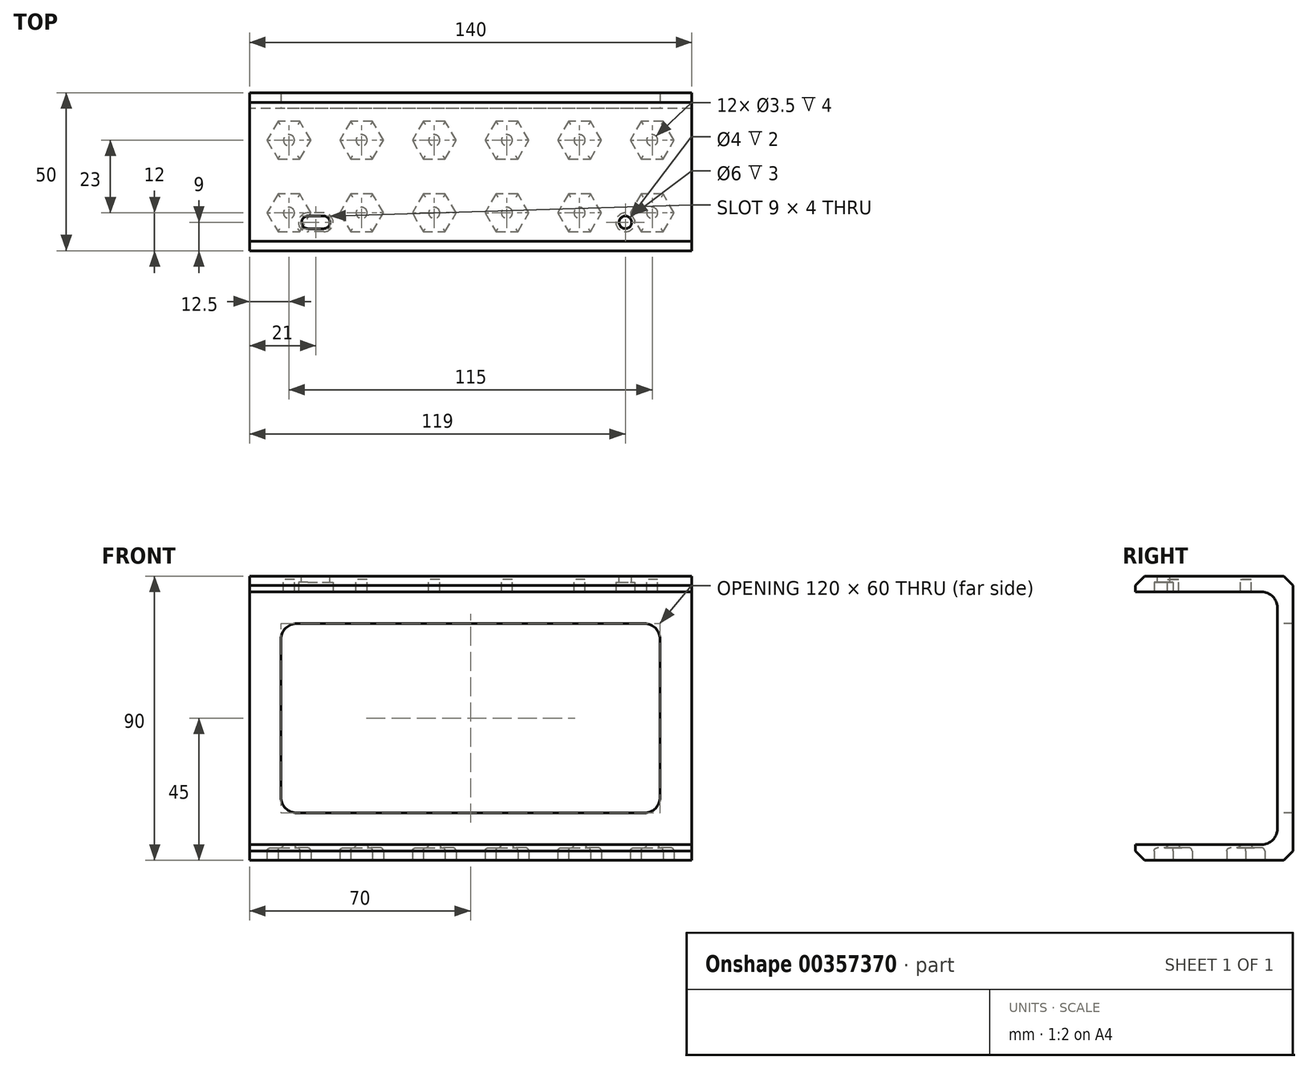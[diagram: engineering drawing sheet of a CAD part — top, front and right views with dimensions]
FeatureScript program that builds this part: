
annotation { "Feature Type Name" : "Feature", "Feature Type Description" : "" }
export const myFeature = defineFeature(function(context is Context, id is Id, definition is map)
    precondition{}
    {
        {
            var Q0;
            Q0=qCreatedBy(makeId("Right.planeOp"),FACE);
            var sketch = newSketch(context, id + "F0", { "sketchPlane" : qUnion([Q0])});
            skLineSegment(sketch, "E0", {"start": v(-50, 0) * mm, "end": v(0, 0) * mm});
            skLineSegment(sketch, "E1", {"start": v(0, 0) * mm, "end": v(0, 90) * mm});
            skLineSegment(sketch, "E2", {"start": v(0, 90) * mm, "end": v(-50, 90) * mm});
            skLineSegment(sketch, "E3", {"start": v(-50, 90) * mm, "end": v(-50, 85) * mm});
            skLineSegment(sketch, "E4", {"start": v(-50, 85) * mm, "end": v(-5, 85) * mm});
            skLineSegment(sketch, "E5", {"start": v(-5, 85) * mm, "end": v(-5, 5) * mm});
            skLineSegment(sketch, "E6", {"start": v(-5, 5) * mm, "end": v(-50, 5) * mm});
            skLineSegment(sketch, "E7", {"start": v(-50, 5) * mm, "end": v(-50, 0) * mm});
            skSolve(sketch);
        }
        {
            var Q0;
            Q0 = qSketchRegion(id + "F0", true);
            extrude(context, id + "F1", {"entities" : qUnion([Q0]), "depth" : 140 * mm});
        }
        {
            var Q0;
            Q0=makeQuery(id+"F1.opExtrude","SWEPT_FACE",FACE,{"disambiguationData":[OSD([sQuery(id+"F0.wireOp",EDGE,"E2")])]});
            cPlane(context, id + "F2", {"entities" : qUnion([Q0]), "cplaneType" : CPlaneType.OFFSET, "offset" : 1 * mm, "oppositeDirection" : true, "width" : 150 * mm, "height" : 150 * mm});
        }
        {
            var Q0;
            Q0=qCreatedBy(id+"F2.planeOp",FACE);
            var sketch = newSketch(context, id + "F3", { "sketchPlane" : qUnion([Q0])});
            skCircle(sketch, "E8", {"center": v(12.5, -38) * mm, "radius": 1.75 * mm});
            skCircle(sketch, "E9", {"center": v(12.5, -38) * mm, "radius": 10 * mm, "construction": true});
            skCircle(sketch, "E10.0.1.0", {"center": v(12.5, -15) * mm, "radius": 10 * mm, "construction": true});
            skCircle(sketch, "E10.0.1.1", {"center": v(12.5, -15) * mm, "radius": 1.75 * mm});
            skCircle(sketch, "E10.1.0.0", {"center": v(35.5, -38) * mm, "radius": 10 * mm, "construction": true});
            skCircle(sketch, "E10.1.0.1", {"center": v(35.5, -38) * mm, "radius": 1.75 * mm});
            skCircle(sketch, "E10.1.1.0", {"center": v(35.5, -15) * mm, "radius": 10 * mm, "construction": true});
            skCircle(sketch, "E10.1.1.1", {"center": v(35.5, -15) * mm, "radius": 1.75 * mm});
            skCircle(sketch, "E10.2.0.0", {"center": v(58.5, -38) * mm, "radius": 10 * mm, "construction": true});
            skCircle(sketch, "E10.2.0.1", {"center": v(58.5, -38) * mm, "radius": 1.75 * mm});
            skCircle(sketch, "E10.2.1.0", {"center": v(58.5, -15) * mm, "radius": 10 * mm, "construction": true});
            skCircle(sketch, "E10.2.1.1", {"center": v(58.5, -15) * mm, "radius": 1.75 * mm});
            skCircle(sketch, "E10.3.0.0", {"center": v(81.5, -38) * mm, "radius": 10 * mm, "construction": true});
            skCircle(sketch, "E10.3.0.1", {"center": v(81.5, -38) * mm, "radius": 1.75 * mm});
            skCircle(sketch, "E10.3.1.0", {"center": v(81.5, -15) * mm, "radius": 10 * mm, "construction": true});
            skCircle(sketch, "E10.3.1.1", {"center": v(81.5, -15) * mm, "radius": 1.75 * mm});
            skCircle(sketch, "E10.4.0.0", {"center": v(104.5, -38) * mm, "radius": 10 * mm, "construction": true});
            skCircle(sketch, "E10.4.0.1", {"center": v(104.5, -38) * mm, "radius": 1.75 * mm});
            skCircle(sketch, "E10.4.1.0", {"center": v(104.5, -15) * mm, "radius": 10 * mm, "construction": true});
            skCircle(sketch, "E10.4.1.1", {"center": v(104.5, -15) * mm, "radius": 1.75 * mm});
            skCircle(sketch, "E10.5.0.0", {"center": v(127.5, -38) * mm, "radius": 10 * mm, "construction": true});
            skCircle(sketch, "E10.5.0.1", {"center": v(127.5, -38) * mm, "radius": 1.75 * mm});
            skCircle(sketch, "E10.5.1.0", {"center": v(127.5, -15) * mm, "radius": 10 * mm, "construction": true});
            skCircle(sketch, "E10.5.1.1", {"center": v(127.5, -15) * mm, "radius": 1.75 * mm});
            skLineSegment(sketch, "E10.direction1", {"start": v(12.5, -38) * mm, "end": v(35.5, -38) * mm, "construction": true});
            skLineSegment(sketch, "E10.direction2", {"start": v(12.5, -38) * mm, "end": v(12.5, -15) * mm, "construction": true});
            skLineSegment(sketch, "E11", {"start": v(70, 0) * mm, "end": v(70, -80.44) * mm, "construction": true});
            skSolve(sketch);
        }
        {
            var Q0;
            Q0 = qSketchRegion(id + "F3", true);
            extrude(context, id + "F4", {"entities" : qUnion([Q0]), "operationType" : NewBodyOperationType.REMOVE, "endBound" : BoundingType.THROUGH_ALL, "oppositeDirection" : true, "depth" : 25 * mm});
        }
        {
            var Q0;
            Q0=makeQuery(id+"F1.opExtrude","SWEPT_FACE",FACE,{"disambiguationData":[OSD([sQuery(id+"F0.wireOp",EDGE,"E0")])]});
            var sketch = newSketch(context, id + "F5", { "sketchPlane" : qUnion([Q0])});
            skCircle(sketch, "E12.cCircle", {"center": v(12.5, 15) * mm, "radius": 6 * mm, "construction": true});
            skLineSegment(sketch, "E12.0", {"start": v(19.43, 15) * mm, "end": v(15.96, 9) * mm});
            skLineSegment(sketch, "E12.1", {"start": v(15.96, 9) * mm, "end": v(9.04, 9) * mm});
            skLineSegment(sketch, "E12.2", {"start": v(9.04, 9) * mm, "end": v(5.57, 15) * mm});
            skLineSegment(sketch, "E12.3", {"start": v(5.57, 15) * mm, "end": v(9.04, 21) * mm});
            skLineSegment(sketch, "E12.4", {"start": v(9.04, 21) * mm, "end": v(15.96, 21) * mm});
            skLineSegment(sketch, "E12.5", {"start": v(15.96, 21) * mm, "end": v(19.43, 15) * mm});
            skPoint(sketch, "E12.0.midPoint", {"position": v(17.7, 12) * mm});
            skLineSegment(sketch, "E13.0.1.0", {"start": v(9.04, 32) * mm, "end": v(5.57, 38) * mm});
            skLineSegment(sketch, "E13.0.1.1", {"start": v(15.96, 32) * mm, "end": v(9.04, 32) * mm});
            skCircle(sketch, "E13.0.1.2", {"center": v(12.5, 38) * mm, "radius": 6 * mm, "construction": true});
            skLineSegment(sketch, "E13.0.1.3", {"start": v(19.43, 38) * mm, "end": v(15.96, 32) * mm});
            skLineSegment(sketch, "E13.0.1.4", {"start": v(15.96, 44) * mm, "end": v(19.43, 38) * mm});
            skLineSegment(sketch, "E13.0.1.5", {"start": v(9.04, 44) * mm, "end": v(15.96, 44) * mm});
            skLineSegment(sketch, "E13.0.1.6", {"start": v(5.57, 38) * mm, "end": v(9.04, 44) * mm});
            skLineSegment(sketch, "E13.1.0.0", {"start": v(32.04, 9) * mm, "end": v(28.57, 15) * mm});
            skLineSegment(sketch, "E13.1.0.1", {"start": v(38.96, 9) * mm, "end": v(32.04, 9) * mm});
            skCircle(sketch, "E13.1.0.2", {"center": v(35.5, 15) * mm, "radius": 6 * mm, "construction": true});
            skLineSegment(sketch, "E13.1.0.3", {"start": v(42.43, 15) * mm, "end": v(38.96, 9) * mm});
            skLineSegment(sketch, "E13.1.0.4", {"start": v(38.96, 21) * mm, "end": v(42.43, 15) * mm});
            skLineSegment(sketch, "E13.1.0.5", {"start": v(32.04, 21) * mm, "end": v(38.96, 21) * mm});
            skLineSegment(sketch, "E13.1.0.6", {"start": v(28.57, 15) * mm, "end": v(32.04, 21) * mm});
            skLineSegment(sketch, "E13.1.1.0", {"start": v(32.04, 32) * mm, "end": v(28.57, 38) * mm});
            skLineSegment(sketch, "E13.1.1.1", {"start": v(38.96, 32) * mm, "end": v(32.04, 32) * mm});
            skCircle(sketch, "E13.1.1.2", {"center": v(35.5, 38) * mm, "radius": 6 * mm, "construction": true});
            skLineSegment(sketch, "E13.1.1.3", {"start": v(42.43, 38) * mm, "end": v(38.96, 32) * mm});
            skLineSegment(sketch, "E13.1.1.4", {"start": v(38.96, 44) * mm, "end": v(42.43, 38) * mm});
            skLineSegment(sketch, "E13.1.1.5", {"start": v(32.04, 44) * mm, "end": v(38.96, 44) * mm});
            skLineSegment(sketch, "E13.1.1.6", {"start": v(28.57, 38) * mm, "end": v(32.04, 44) * mm});
            skLineSegment(sketch, "E13.2.0.0", {"start": v(55.04, 9) * mm, "end": v(51.57, 15) * mm});
            skLineSegment(sketch, "E13.2.0.1", {"start": v(61.96, 9) * mm, "end": v(55.04, 9) * mm});
            skCircle(sketch, "E13.2.0.2", {"center": v(58.5, 15) * mm, "radius": 6 * mm, "construction": true});
            skLineSegment(sketch, "E13.2.0.3", {"start": v(65.43, 15) * mm, "end": v(61.96, 9) * mm});
            skLineSegment(sketch, "E13.2.0.4", {"start": v(61.96, 21) * mm, "end": v(65.43, 15) * mm});
            skLineSegment(sketch, "E13.2.0.5", {"start": v(55.04, 21) * mm, "end": v(61.96, 21) * mm});
            skLineSegment(sketch, "E13.2.0.6", {"start": v(51.57, 15) * mm, "end": v(55.04, 21) * mm});
            skLineSegment(sketch, "E13.2.1.0", {"start": v(55.04, 32) * mm, "end": v(51.57, 38) * mm});
            skLineSegment(sketch, "E13.2.1.1", {"start": v(61.96, 32) * mm, "end": v(55.04, 32) * mm});
            skCircle(sketch, "E13.2.1.2", {"center": v(58.5, 38) * mm, "radius": 6 * mm, "construction": true});
            skLineSegment(sketch, "E13.2.1.3", {"start": v(65.43, 38) * mm, "end": v(61.96, 32) * mm});
            skLineSegment(sketch, "E13.2.1.4", {"start": v(61.96, 44) * mm, "end": v(65.43, 38) * mm});
            skLineSegment(sketch, "E13.2.1.5", {"start": v(55.04, 44) * mm, "end": v(61.96, 44) * mm});
            skLineSegment(sketch, "E13.2.1.6", {"start": v(51.57, 38) * mm, "end": v(55.04, 44) * mm});
            skLineSegment(sketch, "E13.3.0.0", {"start": v(78.04, 9) * mm, "end": v(74.57, 15) * mm});
            skLineSegment(sketch, "E13.3.0.1", {"start": v(84.96, 9) * mm, "end": v(78.04, 9) * mm});
            skCircle(sketch, "E13.3.0.2", {"center": v(81.5, 15) * mm, "radius": 6 * mm, "construction": true});
            skLineSegment(sketch, "E13.3.0.3", {"start": v(88.43, 15) * mm, "end": v(84.96, 9) * mm});
            skLineSegment(sketch, "E13.3.0.4", {"start": v(84.96, 21) * mm, "end": v(88.43, 15) * mm});
            skLineSegment(sketch, "E13.3.0.5", {"start": v(78.04, 21) * mm, "end": v(84.96, 21) * mm});
            skLineSegment(sketch, "E13.3.0.6", {"start": v(74.57, 15) * mm, "end": v(78.04, 21) * mm});
            skLineSegment(sketch, "E13.3.1.0", {"start": v(78.04, 32) * mm, "end": v(74.57, 38) * mm});
            skLineSegment(sketch, "E13.3.1.1", {"start": v(84.96, 32) * mm, "end": v(78.04, 32) * mm});
            skCircle(sketch, "E13.3.1.2", {"center": v(81.5, 38) * mm, "radius": 6 * mm, "construction": true});
            skLineSegment(sketch, "E13.3.1.3", {"start": v(88.43, 38) * mm, "end": v(84.96, 32) * mm});
            skLineSegment(sketch, "E13.3.1.4", {"start": v(84.96, 44) * mm, "end": v(88.43, 38) * mm});
            skLineSegment(sketch, "E13.3.1.5", {"start": v(78.04, 44) * mm, "end": v(84.96, 44) * mm});
            skLineSegment(sketch, "E13.3.1.6", {"start": v(74.57, 38) * mm, "end": v(78.04, 44) * mm});
            skLineSegment(sketch, "E13.4.0.0", {"start": v(101.04, 9) * mm, "end": v(97.57, 15) * mm});
            skLineSegment(sketch, "E13.4.0.1", {"start": v(107.96, 9) * mm, "end": v(101.04, 9) * mm});
            skCircle(sketch, "E13.4.0.2", {"center": v(104.5, 15) * mm, "radius": 6 * mm, "construction": true});
            skLineSegment(sketch, "E13.4.0.3", {"start": v(111.43, 15) * mm, "end": v(107.96, 9) * mm});
            skLineSegment(sketch, "E13.4.0.4", {"start": v(107.96, 21) * mm, "end": v(111.43, 15) * mm});
            skLineSegment(sketch, "E13.4.0.5", {"start": v(101.04, 21) * mm, "end": v(107.96, 21) * mm});
            skLineSegment(sketch, "E13.4.0.6", {"start": v(97.57, 15) * mm, "end": v(101.04, 21) * mm});
            skLineSegment(sketch, "E13.4.1.0", {"start": v(101.04, 32) * mm, "end": v(97.57, 38) * mm});
            skLineSegment(sketch, "E13.4.1.1", {"start": v(107.96, 32) * mm, "end": v(101.04, 32) * mm});
            skCircle(sketch, "E13.4.1.2", {"center": v(104.5, 38) * mm, "radius": 6 * mm, "construction": true});
            skLineSegment(sketch, "E13.4.1.3", {"start": v(111.43, 38) * mm, "end": v(107.96, 32) * mm});
            skLineSegment(sketch, "E13.4.1.4", {"start": v(107.96, 44) * mm, "end": v(111.43, 38) * mm});
            skLineSegment(sketch, "E13.4.1.5", {"start": v(101.04, 44) * mm, "end": v(107.96, 44) * mm});
            skLineSegment(sketch, "E13.4.1.6", {"start": v(97.57, 38) * mm, "end": v(101.04, 44) * mm});
            skLineSegment(sketch, "E13.5.0.0", {"start": v(124.04, 9) * mm, "end": v(120.57, 15) * mm});
            skLineSegment(sketch, "E13.5.0.1", {"start": v(130.96, 9) * mm, "end": v(124.04, 9) * mm});
            skCircle(sketch, "E13.5.0.2", {"center": v(127.5, 15) * mm, "radius": 6 * mm, "construction": true});
            skLineSegment(sketch, "E13.5.0.3", {"start": v(134.43, 15) * mm, "end": v(130.96, 9) * mm});
            skLineSegment(sketch, "E13.5.0.4", {"start": v(130.96, 21) * mm, "end": v(134.43, 15) * mm});
            skLineSegment(sketch, "E13.5.0.5", {"start": v(124.04, 21) * mm, "end": v(130.96, 21) * mm});
            skLineSegment(sketch, "E13.5.0.6", {"start": v(120.57, 15) * mm, "end": v(124.04, 21) * mm});
            skLineSegment(sketch, "E13.5.1.0", {"start": v(124.04, 32) * mm, "end": v(120.57, 38) * mm});
            skLineSegment(sketch, "E13.5.1.1", {"start": v(130.96, 32) * mm, "end": v(124.04, 32) * mm});
            skCircle(sketch, "E13.5.1.2", {"center": v(127.5, 38) * mm, "radius": 6 * mm, "construction": true});
            skLineSegment(sketch, "E13.5.1.3", {"start": v(134.43, 38) * mm, "end": v(130.96, 32) * mm});
            skLineSegment(sketch, "E13.5.1.4", {"start": v(130.96, 44) * mm, "end": v(134.43, 38) * mm});
            skLineSegment(sketch, "E13.5.1.5", {"start": v(124.04, 44) * mm, "end": v(130.96, 44) * mm});
            skLineSegment(sketch, "E13.5.1.6", {"start": v(120.57, 38) * mm, "end": v(124.04, 44) * mm});
            skLineSegment(sketch, "E13.direction1", {"start": v(9.04, 9) * mm, "end": v(32.04, 9) * mm, "construction": true});
            skLineSegment(sketch, "E13.direction2", {"start": v(9.04, 9) * mm, "end": v(9.04, 32) * mm, "construction": true});
            skSolve(sketch);
        }
        {
            var Q0;
            Q0 = qSketchRegion(id + "F5", true);
            extrude(context, id + "F6", {"entities" : qUnion([Q0]), "operationType" : NewBodyOperationType.REMOVE, "oppositeDirection" : true, "depth" : 4 * mm});
        }
        {
            var Q0;
            Q0=makeQuery(id+"F6.boolean.opBoolean","COPY",FACE,{"derivedFrom":makeQuery(id+"F6.opExtrude","CAP_FACE",FACE,{"disambiguationData":[OSD([sQuery(id+"F5.wireOp",EDGE,"E12.0"),sQuery(id+"F5.wireOp",EDGE,"E12.1"),sQuery(id+"F5.wireOp",EDGE,"E12.2"),sQuery(id+"F5.wireOp",EDGE,"E12.3"),sQuery(id+"F5.wireOp",EDGE,"E12.4"),sQuery(id+"F5.wireOp",EDGE,"E12.5")])],"isStart":false})});
            var Q1;
            Q1=makeQuery(id+"F6.boolean.opBoolean","COPY",FACE,{"derivedFrom":makeQuery(id+"F6.opExtrude","CAP_FACE",FACE,{"disambiguationData":[OSD([sQuery(id+"F5.wireOp",EDGE,"E13.0.1.0"),sQuery(id+"F5.wireOp",EDGE,"E13.0.1.1"),sQuery(id+"F5.wireOp",EDGE,"E13.0.1.3"),sQuery(id+"F5.wireOp",EDGE,"E13.0.1.4"),sQuery(id+"F5.wireOp",EDGE,"E13.0.1.5"),sQuery(id+"F5.wireOp",EDGE,"E13.0.1.6")])],"isStart":false})});
            var Q2;
            Q2=makeQuery(id+"F6.boolean.opBoolean","COPY",FACE,{"derivedFrom":makeQuery(id+"F6.opExtrude","CAP_FACE",FACE,{"disambiguationData":[OSD([sQuery(id+"F5.wireOp",EDGE,"E13.1.0.0"),sQuery(id+"F5.wireOp",EDGE,"E13.1.0.1"),sQuery(id+"F5.wireOp",EDGE,"E13.1.0.3"),sQuery(id+"F5.wireOp",EDGE,"E13.1.0.4"),sQuery(id+"F5.wireOp",EDGE,"E13.1.0.5"),sQuery(id+"F5.wireOp",EDGE,"E13.1.0.6")])],"isStart":false})});
            var Q3;
            Q3=makeQuery(id+"F6.boolean.opBoolean","COPY",FACE,{"derivedFrom":makeQuery(id+"F6.opExtrude","CAP_FACE",FACE,{"disambiguationData":[OSD([sQuery(id+"F5.wireOp",EDGE,"E13.1.1.0"),sQuery(id+"F5.wireOp",EDGE,"E13.1.1.1"),sQuery(id+"F5.wireOp",EDGE,"E13.1.1.3"),sQuery(id+"F5.wireOp",EDGE,"E13.1.1.4"),sQuery(id+"F5.wireOp",EDGE,"E13.1.1.5"),sQuery(id+"F5.wireOp",EDGE,"E13.1.1.6")])],"isStart":false})});
            var Q4;
            Q4=makeQuery(id+"F6.boolean.opBoolean","COPY",FACE,{"derivedFrom":makeQuery(id+"F6.opExtrude","CAP_FACE",FACE,{"disambiguationData":[OSD([sQuery(id+"F5.wireOp",EDGE,"E13.2.0.0"),sQuery(id+"F5.wireOp",EDGE,"E13.2.0.1"),sQuery(id+"F5.wireOp",EDGE,"E13.2.0.3"),sQuery(id+"F5.wireOp",EDGE,"E13.2.0.4"),sQuery(id+"F5.wireOp",EDGE,"E13.2.0.5"),sQuery(id+"F5.wireOp",EDGE,"E13.2.0.6")])],"isStart":false})});
            var Q5;
            Q5=makeQuery(id+"F6.boolean.opBoolean","COPY",FACE,{"derivedFrom":makeQuery(id+"F6.opExtrude","CAP_FACE",FACE,{"disambiguationData":[OSD([sQuery(id+"F5.wireOp",EDGE,"E13.2.1.0"),sQuery(id+"F5.wireOp",EDGE,"E13.2.1.1"),sQuery(id+"F5.wireOp",EDGE,"E13.2.1.3"),sQuery(id+"F5.wireOp",EDGE,"E13.2.1.4"),sQuery(id+"F5.wireOp",EDGE,"E13.2.1.5"),sQuery(id+"F5.wireOp",EDGE,"E13.2.1.6")])],"isStart":false})});
            var Q6;
            Q6=makeQuery(id+"F6.boolean.opBoolean","COPY",FACE,{"derivedFrom":makeQuery(id+"F6.opExtrude","CAP_FACE",FACE,{"disambiguationData":[OSD([sQuery(id+"F5.wireOp",EDGE,"E13.3.1.0"),sQuery(id+"F5.wireOp",EDGE,"E13.3.1.1"),sQuery(id+"F5.wireOp",EDGE,"E13.3.1.3"),sQuery(id+"F5.wireOp",EDGE,"E13.3.1.4"),sQuery(id+"F5.wireOp",EDGE,"E13.3.1.5"),sQuery(id+"F5.wireOp",EDGE,"E13.3.1.6")])],"isStart":false})});
            var Q7;
            Q7=makeQuery(id+"F6.boolean.opBoolean","COPY",FACE,{"derivedFrom":makeQuery(id+"F6.opExtrude","CAP_FACE",FACE,{"disambiguationData":[OSD([sQuery(id+"F5.wireOp",EDGE,"E13.3.0.0"),sQuery(id+"F5.wireOp",EDGE,"E13.3.0.1"),sQuery(id+"F5.wireOp",EDGE,"E13.3.0.3"),sQuery(id+"F5.wireOp",EDGE,"E13.3.0.4"),sQuery(id+"F5.wireOp",EDGE,"E13.3.0.5"),sQuery(id+"F5.wireOp",EDGE,"E13.3.0.6")])],"isStart":false})});
            var Q8;
            Q8=makeQuery(id+"F6.boolean.opBoolean","COPY",FACE,{"derivedFrom":makeQuery(id+"F6.opExtrude","CAP_FACE",FACE,{"disambiguationData":[OSD([sQuery(id+"F5.wireOp",EDGE,"E13.4.0.0"),sQuery(id+"F5.wireOp",EDGE,"E13.4.0.1"),sQuery(id+"F5.wireOp",EDGE,"E13.4.0.3"),sQuery(id+"F5.wireOp",EDGE,"E13.4.0.4"),sQuery(id+"F5.wireOp",EDGE,"E13.4.0.5"),sQuery(id+"F5.wireOp",EDGE,"E13.4.0.6")])],"isStart":false})});
            var Q9;
            Q9=makeQuery(id+"F6.boolean.opBoolean","COPY",FACE,{"derivedFrom":makeQuery(id+"F6.opExtrude","CAP_FACE",FACE,{"disambiguationData":[OSD([sQuery(id+"F5.wireOp",EDGE,"E13.4.1.0"),sQuery(id+"F5.wireOp",EDGE,"E13.4.1.1"),sQuery(id+"F5.wireOp",EDGE,"E13.4.1.3"),sQuery(id+"F5.wireOp",EDGE,"E13.4.1.4"),sQuery(id+"F5.wireOp",EDGE,"E13.4.1.5"),sQuery(id+"F5.wireOp",EDGE,"E13.4.1.6")])],"isStart":false})});
            var Q10;
            Q10=makeQuery(id+"F6.boolean.opBoolean","COPY",FACE,{"derivedFrom":makeQuery(id+"F6.opExtrude","CAP_FACE",FACE,{"disambiguationData":[OSD([sQuery(id+"F5.wireOp",EDGE,"E13.5.1.0"),sQuery(id+"F5.wireOp",EDGE,"E13.5.1.1"),sQuery(id+"F5.wireOp",EDGE,"E13.5.1.3"),sQuery(id+"F5.wireOp",EDGE,"E13.5.1.4"),sQuery(id+"F5.wireOp",EDGE,"E13.5.1.5"),sQuery(id+"F5.wireOp",EDGE,"E13.5.1.6")])],"isStart":false})});
            var Q11;
            Q11=makeQuery(id+"F6.boolean.opBoolean","COPY",FACE,{"derivedFrom":makeQuery(id+"F6.opExtrude","CAP_FACE",FACE,{"disambiguationData":[OSD([sQuery(id+"F5.wireOp",EDGE,"E13.5.0.0"),sQuery(id+"F5.wireOp",EDGE,"E13.5.0.1"),sQuery(id+"F5.wireOp",EDGE,"E13.5.0.3"),sQuery(id+"F5.wireOp",EDGE,"E13.5.0.4"),sQuery(id+"F5.wireOp",EDGE,"E13.5.0.5"),sQuery(id+"F5.wireOp",EDGE,"E13.5.0.6")])],"isStart":false})});
            fillet(context, id + "F7", {"entities" : qUnion([Q0, Q1, Q2, Q3, Q4, Q5, Q6, Q7, Q8, Q9, Q10, Q11]), "radius" : 1 * mm, "tangentPropagation" : true, "allowEdgeOverflow" : false});
        }
        {
            var Q0;
            Q0=makeQuery(id+"F1.opExtrude","SWEPT_EDGE",EDGE,{"disambiguationData":[OSD([sQuery(id+"F0.wireOp",EDGE,"E5"),sQuery(id+"F0.wireOp",EDGE,"E6")])]});
            var Q1;
            Q1=makeQuery(id+"F1.opExtrude","SWEPT_EDGE",EDGE,{"disambiguationData":[OSD([sQuery(id+"F0.wireOp",EDGE,"E4"),sQuery(id+"F0.wireOp",EDGE,"E5")])]});
            fillet(context, id + "F8", {"entities" : qUnion([Q0, Q1]), "radius" : 5 * mm, "tangentPropagation" : true, "allowEdgeOverflow" : false});
        }
        {
            var Q0;
            Q0=makeQuery(id+"F1.opExtrude","SWEPT_EDGE",EDGE,{"disambiguationData":[OSD([sQuery(id+"F0.wireOp",EDGE,"E1"),sQuery(id+"F0.wireOp",EDGE,"E2")])]});
            var Q1;
            Q1=makeQuery(id+"F1.opExtrude","SWEPT_EDGE",EDGE,{"disambiguationData":[OSD([sQuery(id+"F0.wireOp",EDGE,"E2"),sQuery(id+"F0.wireOp",EDGE,"E3")])]});
            var Q2;
            Q2=makeQuery(id+"F1.opExtrude","SWEPT_EDGE",EDGE,{"disambiguationData":[OSD([sQuery(id+"F0.wireOp",EDGE,"E0"),sQuery(id+"F0.wireOp",EDGE,"E1")])]});
            var Q3;
            Q3=makeQuery(id+"F1.opExtrude","SWEPT_EDGE",EDGE,{"disambiguationData":[OSD([sQuery(id+"F0.wireOp",EDGE,"E0"),sQuery(id+"F0.wireOp",EDGE,"E7")])]});
            chamfer(context, id + "F9", {"entities" : qUnion([Q0, Q1, Q2, Q3]), "width" : 3 * mm, "tangentPropagation" : true});
        }
        {
            var Q0;
            Q0=makeQuery(id+"F1.opExtrude","SWEPT_FACE",FACE,{"disambiguationData":[OSD([sQuery(id+"F0.wireOp",EDGE,"E2")])]});
            var sketch = newSketch(context, id + "F10", { "sketchPlane" : qUnion([Q0])});
            skLineSegment(sketch, "E14.0", {"start": v(70, 0) * mm, "end": v(70, -80.44) * mm, "construction": true});
            skSolve(sketch);
        }
        {
            var Q0;
            Q0=makeQuery(id+"F1.opExtrude","SWEPT_FACE",FACE,{"disambiguationData":[OSD([sQuery(id+"F0.wireOp",EDGE,"E5")])]});
            var sketch = newSketch(context, id + "F11", { "sketchPlane" : qUnion([Q0])});
            skLineSegment(sketch, "E15.bottom", {"start": v(130, 15) * mm, "end": v(10, 15) * mm});
            skLineSegment(sketch, "E15.top", {"start": v(130, 75) * mm, "end": v(10, 75) * mm});
            skLineSegment(sketch, "E15.left", {"start": v(130, 15) * mm, "end": v(130, 75) * mm});
            skLineSegment(sketch, "E15.right", {"start": v(10, 15) * mm, "end": v(10, 75) * mm});
            skPoint(sketch, "E15.middle", {"position": v(70, 45) * mm});
            skLineSegment(sketch, "E16", {"start": v(70, 90) * mm, "end": v(70, -40.93) * mm, "construction": true});
            skLineSegment(sketch, "E17", {"start": v(140, 45) * mm, "end": v(0, 45) * mm, "construction": true});
            skSolve(sketch);
        }
        {
            var Q0;
            Q0 = qSketchRegion(id + "F11", true);
            extrude(context, id + "F12", {"entities" : qUnion([Q0]), "operationType" : NewBodyOperationType.REMOVE, "endBound" : BoundingType.THROUGH_ALL, "oppositeDirection" : true, "depth" : 25 * mm});
        }
        {
            var Q0;
            Q0=makeQuery(id+"F12.boolean.opBoolean","COPY",EDGE,{"derivedFrom":makeQuery(id+"F12.opExtrude","SWEPT_EDGE",EDGE,{"disambiguationData":[OSD([sQuery(id+"F11.wireOp",EDGE,"E15.bottom"),sQuery(id+"F11.wireOp",EDGE,"E15.left")])]})});
            var Q1;
            Q1=makeQuery(id+"F12.boolean.opBoolean","COPY",EDGE,{"derivedFrom":makeQuery(id+"F12.opExtrude","SWEPT_EDGE",EDGE,{"disambiguationData":[OSD([sQuery(id+"F11.wireOp",EDGE,"E15.bottom"),sQuery(id+"F11.wireOp",EDGE,"E15.right")])]})});
            var Q2;
            Q2=makeQuery(id+"F12.boolean.opBoolean","COPY",EDGE,{"derivedFrom":makeQuery(id+"F12.opExtrude","SWEPT_EDGE",EDGE,{"disambiguationData":[OSD([sQuery(id+"F11.wireOp",EDGE,"E15.top"),sQuery(id+"F11.wireOp",EDGE,"E15.left")])]})});
            var Q3;
            Q3=makeQuery(id+"F12.boolean.opBoolean","COPY",EDGE,{"derivedFrom":makeQuery(id+"F12.opExtrude","SWEPT_EDGE",EDGE,{"disambiguationData":[OSD([sQuery(id+"F11.wireOp",EDGE,"E15.top"),sQuery(id+"F11.wireOp",EDGE,"E15.right")])]})});
            fillet(context, id + "F13", {"entities" : qUnion([Q0, Q1, Q2, Q3]), "radius" : 5 * mm, "tangentPropagation" : true, "allowEdgeOverflow" : false});
        }
        {
            var Q0;
            {var subQ0=sQuery(id+"F0.wireOp",EDGE,"E2");Q0=makeQuery(id+"F10.imprint","IMPRINT",FACE,{"disambiguationData":[TD([[makeQuery(id+"F10.imprint","IMPRINT",EDGE,{"derivedFrom":makeQuery(id+"F1.opExtrude","CAP_EDGE",EDGE,{"disambiguationData":[OSD([subQ0])],"isStart":true})}),1.0]])]});}
            var sketch = newSketch(context, id + "F14", { "sketchPlane" : qUnion([Q0])});
            skCircle(sketch, "E18", {"center": v(119, -41) * mm, "radius": 2 * mm});
            skLineSegment(sketch, "E19", {"start": v(18.5, -41) * mm, "end": v(23.5, -41) * mm, "construction": true});
            skArc(sketch, "E20.0.startCap", {"start": v(18.5, -43) * mm, "mid": v(16.5, -41) * mm, "end": v(18.5, -39) * mm});
            skArc(sketch, "E20.0.endCap", {"start": v(23.5, -39) * mm, "mid": v(25.5, -41) * mm, "end": v(23.5, -43) * mm});
            skLineSegment(sketch, "E20.0.left", {"start": v(18.5, -39) * mm, "end": v(23.5, -39) * mm});
            skLineSegment(sketch, "E20.0.right", {"start": v(18.5, -43) * mm, "end": v(23.5, -43) * mm});
            skLineSegment(sketch, "E21", {"start": v(21, -41) * mm, "end": v(21, -54.29) * mm, "construction": true});
            skSolve(sketch);
        }
        {
            var Q0;
            Q0 = qSketchRegion(id + "F14", true);
            var Q1;
            Q1=makeQuery(id+"F1.opExtrude","SWEPT_FACE",FACE,{"disambiguationData":[OSD([sQuery(id+"F0.wireOp",EDGE,"E4")])]});
            extrude(context, id + "F15", {"entities" : qUnion([Q0]), "operationType" : NewBodyOperationType.REMOVE, "endBound" : BoundingType.UP_TO_SURFACE, "oppositeDirection" : true, "endBoundEntityFace" : qUnion([Q1]), "depth" : 25 * mm});
        }
        {
            var Q0;
            Q0=makeQuery(id+"F1.opExtrude","SWEPT_FACE",FACE,{"disambiguationData":[OSD([sQuery(id+"F0.wireOp",EDGE,"E4")])]});
            var sketch = newSketch(context, id + "F16", { "sketchPlane" : qUnion([Q0])});
            skCircle(sketch, "E22.0", {"center": v(119, 41) * mm, "radius": 2 * mm, "construction": true});
            skArc(sketch, "E23.0", {"start": v(18.5, 39) * mm, "mid": v(16.5, 41) * mm, "end": v(18.5, 43) * mm, "construction": true});
            skLineSegment(sketch, "E24.0", {"start": v(23.5, 43) * mm, "end": v(18.5, 43) * mm, "construction": true});
            skArc(sketch, "E25.0", {"start": v(23.5, 43) * mm, "mid": v(25.5, 41) * mm, "end": v(23.5, 39) * mm, "construction": true});
            skCircle(sketch, "E26.0", {"center": v(119, 41) * mm, "radius": 3 * mm});
            skLineSegment(sketch, "E27.0", {"start": v(23.5, 39) * mm, "end": v(18.5, 39) * mm, "construction": true});
            skLineSegment(sketch, "E28", {"start": v(23.5, 41) * mm, "end": v(18.5, 41) * mm, "construction": true});
            skArc(sketch, "E29.0.startCap", {"start": v(23.5, 44) * mm, "mid": v(26.5, 41) * mm, "end": v(23.5, 38) * mm});
            skArc(sketch, "E29.0.endCap", {"start": v(18.5, 38) * mm, "mid": v(15.5, 41) * mm, "end": v(18.5, 44) * mm});
            skLineSegment(sketch, "E29.0.left", {"start": v(23.5, 38) * mm, "end": v(18.5, 38) * mm});
            skLineSegment(sketch, "E29.0.right", {"start": v(23.5, 44) * mm, "end": v(18.5, 44) * mm});
            skSolve(sketch);
        }
        {
            var Q0;
            Q0 = qSketchRegion(id + "F16", true);
            extrude(context, id + "F17", {"entities" : qUnion([Q0]), "operationType" : NewBodyOperationType.REMOVE, "oppositeDirection" : true, "depth" : 3 * mm});
        }
    });
